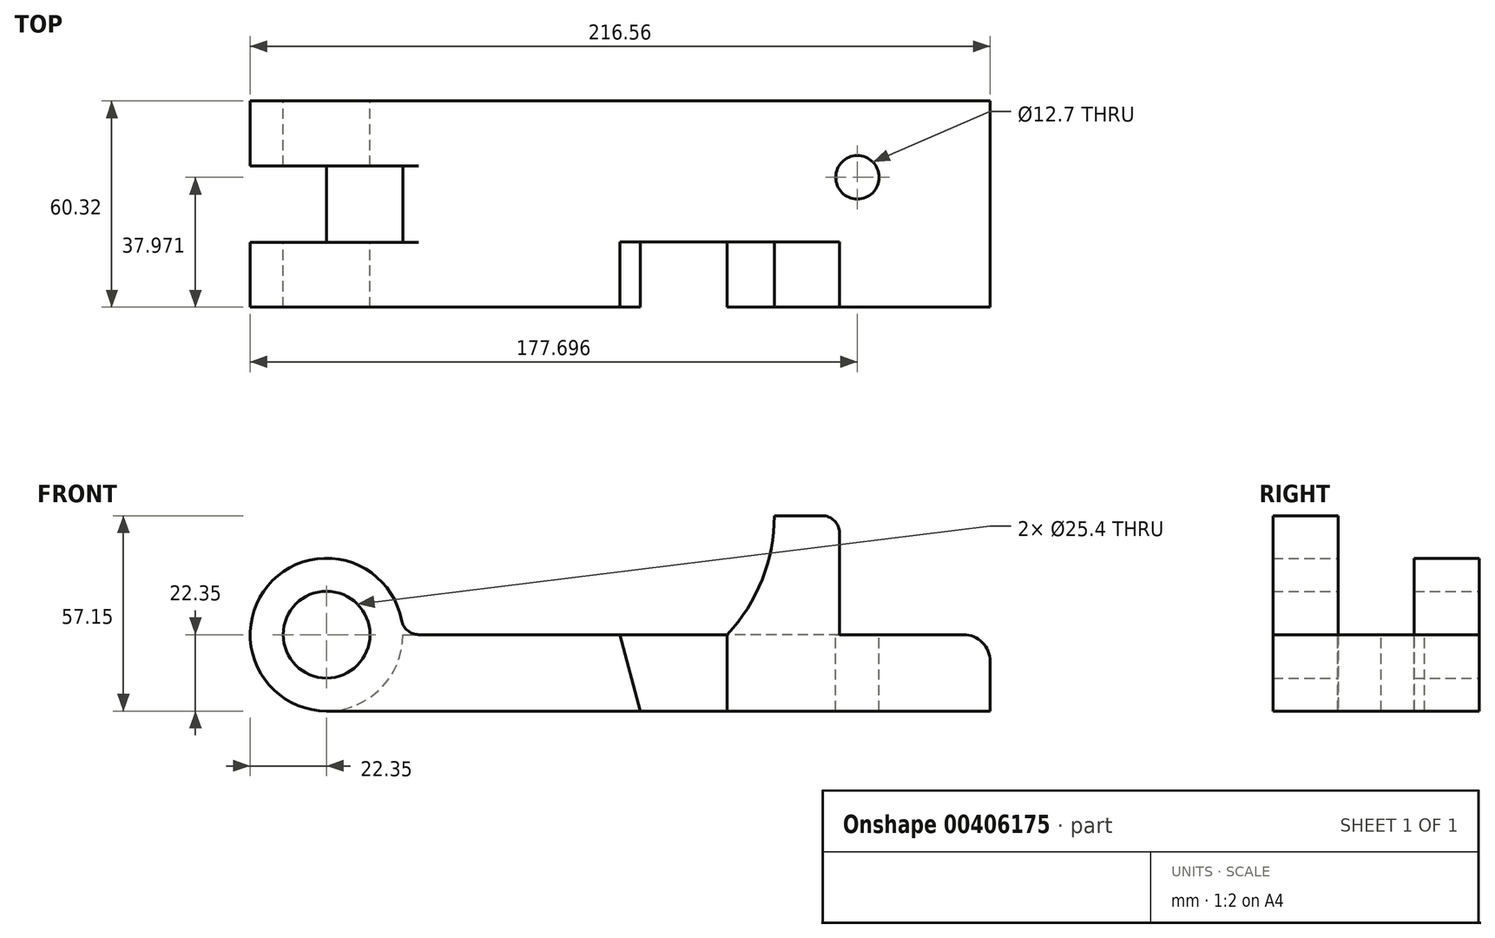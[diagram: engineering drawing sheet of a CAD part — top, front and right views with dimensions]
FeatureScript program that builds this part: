
annotation { "Feature Type Name" : "Feature", "Feature Type Description" : "" }
export const myFeature = defineFeature(function(context is Context, id is Id, definition is map)
    precondition{}
    {
        {
            var Q0;
            Q0=qCreatedBy(makeId("Front.planeOp"),FACE);
            var sketch = newSketch(context, id + "F0", { "sketchPlane" : qUnion([Q0])});
            skLineSegment(sketch, "E0.bottom", {"start": v(194.2, 0) * mm, "end": v(0, 0) * mm});
            skLineSegment(sketch, "E0.top", {"start": v(194.2, -22.35) * mm, "end": v(0, -22.35) * mm});
            skLineSegment(sketch, "E0.left", {"start": v(194.2, 0) * mm, "end": v(194.2, -22.35) * mm});
            skLineSegment(sketch, "E0.right", {"start": v(0, 0) * mm, "end": v(0, -22.35) * mm});
            skLineSegment(sketch, "E1.bottom", {"start": v(131.04, 0) * mm, "end": v(150.09, 0) * mm});
            skLineSegment(sketch, "E1.top", {"start": v(131.04, 34.8) * mm, "end": v(150.09, 34.8) * mm});
            skLineSegment(sketch, "E1.left", {"start": v(131.04, 0) * mm, "end": v(131.04, 34.8) * mm});
            skLineSegment(sketch, "E1.right", {"start": v(150.09, 0) * mm, "end": v(150.09, 34.8) * mm});
            skLineSegment(sketch, "E2", {"start": v(43.97, 0) * mm, "end": v(64.88, -22.35) * mm});
            skLineSegment(sketch, "E3", {"start": v(85.85, 0) * mm, "end": v(91.85, -22.35) * mm});
            skLineSegment(sketch, "E4", {"start": v(91.85, -22.35) * mm, "end": v(91.85, 0) * mm});
            skLineSegment(sketch, "E5", {"start": v(91.85, 0) * mm, "end": v(97.84, -22.35) * mm});
            skArc(sketch, "E6", {"start": v(117.25, 0) * mm, "mid": v(127.47, 16.08) * mm, "end": v(131.04, 34.8) * mm});
            skLineSegment(sketch, "E7", {"start": v(117.25, 0) * mm, "end": v(117.25, -22.35) * mm});
            skCircle(sketch, "E8", {"center": v(0, 0) * mm, "radius": 12.7 * mm});
            skCircle(sketch, "E9", {"center": v(0, 0) * mm, "radius": 22.35 * mm});
            skSolve(sketch);
        }
        {
            var Q0;
            {var subQ0=sQuery(id+"F0.wireOp",EDGE,"E5");Q0=makeQuery(id+"F0.imprint","IMPRINT",FACE,{"disambiguationData":[TD([[makeQuery(id+"F0.imprint","IMPRINT",EDGE,{"derivedFrom":subQ0}),1.0]])]});}
            var Q1;
            {var subQ0=sQuery(id+"F0.wireOp",EDGE,"E3");Q1=makeQuery(id+"F0.imprint","IMPRINT",FACE,{"disambiguationData":[TD([[makeQuery(id+"F0.imprint","IMPRINT",EDGE,{"derivedFrom":subQ0}),1.0]])]});}
            var Q2;
            {var subQ0=sQuery(id+"F0.wireOp",EDGE,"E2");Q2=makeQuery(id+"F0.imprint","IMPRINT",FACE,{"disambiguationData":[TD([[makeQuery(id+"F0.imprint","IMPRINT",EDGE,{"derivedFrom":subQ0}),1.0]])]});}
            var Q3;
            {var subQ0=sQuery(id+"F0.wireOp",EDGE,"E2");Q3=makeQuery(id+"F0.imprint","IMPRINT",FACE,{"disambiguationData":[TD([[makeQuery(id+"F0.imprint","IMPRINT",EDGE,{"derivedFrom":subQ0}),-1.0]])]});}
            var Q4;
            {var subQ0=sQuery(id+"F0.wireOp",EDGE,"E9");var subQ1=sQuery(id+"F0.wireOp",EDGE,"E0.bottom");var subQ2=makeQuery(id+"F0.imprint","INTERSECT",VERTEX,{"derivedFrom":[subQ1,subQ0]});Q4=makeQuery(id+"F0.imprint","IMPRINT",FACE,{"disambiguationData":[TD([[makeQuery(id+"F0.imprint","IMPRINT",EDGE,{"disambiguationData":[TD([[subQ2,-1.0]])],"derivedFrom":subQ1}),-1.0]])]});}
            var Q5;
            {var subQ0=sQuery(id+"F0.wireOp",EDGE,"E4");Q5=makeQuery(id+"F0.imprint","IMPRINT",FACE,{"disambiguationData":[TD([[makeQuery(id+"F0.imprint","IMPRINT",EDGE,{"derivedFrom":subQ0}),-1.0]])]});}
            var Q6;
            {var subQ0=sQuery(id+"F0.wireOp",EDGE,"E0.left");Q6=makeQuery(id+"F0.imprint","IMPRINT",FACE,{"disambiguationData":[TD([[makeQuery(id+"F0.imprint","IMPRINT",EDGE,{"derivedFrom":subQ0}),-1.0]])]});}
            var Q7;
            {var subQ0=sQuery(id+"F0.wireOp",EDGE,"E9");var subQ1=sQuery(id+"F0.wireOp",EDGE,"E0.bottom");var subQ2=makeQuery(id+"F0.imprint","INTERSECT",VERTEX,{"derivedFrom":[subQ1,subQ0]});Q7=makeQuery(id+"F0.imprint","IMPRINT",FACE,{"disambiguationData":[TD([[makeQuery(id+"F0.imprint","IMPRINT",EDGE,{"disambiguationData":[TD([[subQ2,-1.0]])],"derivedFrom":subQ1}),1.0]])]});}
            extrude(context, id + "F1", {"entities" : qUnion([Q0, Q1, Q2, Q3, Q4, Q5, Q6, Q7]), "endBound" : BoundingType.SYMMETRIC, "depth" : 60.32 * mm});
        }
        {
            var Q0;
            {var subQ0=sQuery(id+"F0.wireOp",EDGE,"E9");var subQ1=sQuery(id+"F0.wireOp",EDGE,"E0.bottom");var subQ2=makeQuery(id+"F0.imprint","INTERSECT",VERTEX,{"derivedFrom":[subQ1,subQ0]});Q0=makeQuery(id+"F0.imprint","IMPRINT",FACE,{"disambiguationData":[TD([[makeQuery(id+"F0.imprint","IMPRINT",EDGE,{"disambiguationData":[TD([[subQ2,-1.0]])],"derivedFrom":subQ1}),-1.0]])]});}
            var Q1;
            {var subQ0=sQuery(id+"F0.wireOp",EDGE,"E9");var subQ1=sQuery(id+"F0.wireOp",EDGE,"E0.bottom");var subQ2=makeQuery(id+"F0.imprint","INTERSECT",VERTEX,{"derivedFrom":[subQ1,subQ0]});Q1=makeQuery(id+"F0.imprint","IMPRINT",FACE,{"disambiguationData":[TD([[makeQuery(id+"F0.imprint","IMPRINT",EDGE,{"disambiguationData":[TD([[subQ2,-1.0]])],"derivedFrom":subQ1}),1.0]])]});}
            extrude(context, id + "F2", {"entities" : qUnion([Q0, Q1]), "operationType" : NewBodyOperationType.REMOVE, "endBound" : BoundingType.SYMMETRIC, "oppositeDirection" : true, "depth" : 22.33 * mm});
        }
        {
            var Q0;
            Q0=makeQuery(id+"F1.opExtrude","CAP_FACE",FACE,{"disambiguationData":[OSD([sQuery(id+"F0.wireOp",EDGE,"E0.bottom"),sQuery(id+"F0.wireOp",EDGE,"E0.top"),sQuery(id+"F0.wireOp",EDGE,"E0.left"),sQuery(id+"F0.wireOp",EDGE,"E1.top"),sQuery(id+"F0.wireOp",EDGE,"E1.right"),sQuery(id+"F0.wireOp",EDGE,"E6"),sQuery(id+"F0.wireOp",EDGE,"E8"),sQuery(id+"F0.wireOp",EDGE,"E9")])],"isStart":false});
            var sketch = newSketch(context, id + "F3", { "sketchPlane" : qUnion([Q0])});
            skLineSegment(sketch, "E10.0", {"start": v(117.25, 0) * mm, "end": v(117.25, -22.35) * mm});
            skLineSegment(sketch, "E11.0", {"start": v(85.85, 0) * mm, "end": v(91.85, -22.35) * mm});
            skLineSegment(sketch, "E12", {"start": v(85.85, 0) * mm, "end": v(117.25, 0) * mm});
            skLineSegment(sketch, "E13", {"start": v(91.85, -22.35) * mm, "end": v(117.25, -22.35) * mm});
            skLineSegment(sketch, "E14.0", {"start": v(150.09, 0) * mm, "end": v(150.09, 34.8) * mm});
            skPoint(sketch, "E15.0", {"position": v(140.56, 34.8) * mm});
            skLineSegment(sketch, "E16.0", {"start": v(131.04, 34.8) * mm, "end": v(150.09, 34.8) * mm});
            skArc(sketch, "E17.0", {"start": v(117.25, 0) * mm, "mid": v(127.47, 16.08) * mm, "end": v(131.04, 34.8) * mm});
            skLineSegment(sketch, "E18.0", {"start": v(194.2, 0) * mm, "end": v(0, 0) * mm});
            skSolve(sketch);
        }
        {
            var Q0;
            Q0=makeQuery(id+"F3.imprint","IMPRINT",FACE,{"disambiguationData":[TD([[makeQuery(id+"F3.imprint","IMPRINT",EDGE,{"derivedFrom":sQuery(id+"F3.wireOp",EDGE,"E10.0")}),-1.0]])]});
            extrude(context, id + "F4", {"entities" : qUnion([Q0]), "operationType" : NewBodyOperationType.REMOVE, "oppositeDirection" : true, "depth" : 19.05 * mm});
        }
        {
            var Q0;
            {var subQ0=sQuery(id+"F3.wireOp",EDGE,"E14.0");Q0=makeQuery(id+"F3.imprint","IMPRINT",FACE,{"disambiguationData":[TD([[makeQuery(id+"F3.imprint","IMPRINT",EDGE,{"derivedFrom":subQ0}),1.0]])]});}
            extrude(context, id + "F5", {"entities" : qUnion([Q0]), "operationType" : NewBodyOperationType.ADD, "oppositeDirection" : true, "depth" : 19.05 * mm});
        }
        {
            var Q0;
            Q0=makeQuery(id+"F1.opExtrude","SWEPT_EDGE",EDGE,{"disambiguationData":[OSD([sQuery(id+"F0.wireOp",EDGE,"E0.bottom"),sQuery(id+"F0.wireOp",EDGE,"E0.left")])]});
            fillet(context, id + "F6", {"entities" : qUnion([Q0]), "radius" : 7.87 * mm, "tangentPropagation" : true, "allowEdgeOverflow" : false});
        }
        {
            var Q0;
            Q0=makeQuery(id+"F5.opExtrude","SWEPT_EDGE",EDGE,{"disambiguationData":[OSD([sQuery(id+"F3.wireOp",EDGE,"E14.0"),sQuery(id+"F3.wireOp",EDGE,"E16.0")])]});
            var Q1;
            Q1=makeQuery(id+"F5.opExtrude","SWEPT_EDGE",EDGE,{"disambiguationData":[OSD([sQuery(id+"F3.wireOp",EDGE,"E14.0"),sQuery(id+"F3.wireOp",EDGE,"E18.0")])]});
            var Q2;
            {var subQ0=sQuery(id+"F0.wireOp",EDGE,"E9");var subQ1=sQuery(id+"F0.wireOp",EDGE,"E8");var subQ2=makeQuery(id+"F1.opExtrude","SWEPT_FACE",FACE,{"disambiguationData":[OSD([subQ0])]});var subQ3=sQuery(id+"F0.wireOp",EDGE,"E1.bottom");var subQ4=sQuery(id+"F0.wireOp",EDGE,"E0.bottom");var subQ5=makeQuery(id+"F1.opExtrude","SWEPT_FACE",FACE,{"disambiguationData":[OSD([subQ4,subQ3])]});Q2=makeQuery(id+"F2.boolean.opBoolean","SPLIT",EDGE,{"disambiguationData":[topologyDisambiguationEdgeConnected([subQ5,subQ2]),TD([makeQuery(id+"F2.opExtrude","CAP_FACE",FACE,{"disambiguationData":[OSD([subQ1,subQ0])],"isStart":false})])],"derivedFrom":makeQuery(id+"F1.opExtrude","SWEPT_EDGE",EDGE,{"disambiguationData":[OSD([subQ4,subQ0])]})});}
            var Q3;
            {var subQ0=sQuery(id+"F0.wireOp",EDGE,"E9");var subQ1=sQuery(id+"F0.wireOp",EDGE,"E8");var subQ2=sQuery(id+"F0.wireOp",EDGE,"E1.bottom");var subQ3=sQuery(id+"F0.wireOp",EDGE,"E0.bottom");var subQ4=makeQuery(id+"F1.opExtrude","SWEPT_FACE",FACE,{"disambiguationData":[OSD([subQ3,subQ2])]});var subQ5=makeQuery(id+"F1.opExtrude","SWEPT_FACE",FACE,{"disambiguationData":[OSD([subQ0])]});Q3=makeQuery(id+"F2.boolean.opBoolean","SPLIT",EDGE,{"disambiguationData":[topologyDisambiguationEdgeConnected([subQ4,subQ5]),TD([makeQuery(id+"F2.opExtrude","CAP_FACE",FACE,{"disambiguationData":[OSD([subQ1,subQ0])],"isStart":true})])],"derivedFrom":makeQuery(id+"F1.opExtrude","SWEPT_EDGE",EDGE,{"disambiguationData":[OSD([subQ3,subQ0])]})});}
            fillet(context, id + "F7", {"entities" : qUnion([Q0, Q1, Q2, Q3]), "radius" : 5.08 * mm, "tangentPropagation" : true, "allowEdgeOverflow" : false});
        }
        {
            var Q0;
            Q0=makeQuery(id+"F1.opExtrude","SWEPT_FACE",FACE,{"disambiguationData":[OSD([sQuery(id+"F0.wireOp",EDGE,"E0.bottom"),sQuery(id+"F0.wireOp",EDGE,"E1.bottom")])]});
            var sketch = newSketch(context, id + "F8", { "sketchPlane" : qUnion([Q0])});
            skCircle(sketch, "E19", {"center": v(155.35, 7.81) * mm, "radius": 6.35 * mm});
            skSolve(sketch);
        }
        {
            var Q0;
            Q0=makeQuery(id+"F8.imprint","IMPRINT",FACE,{"disambiguationData":[TD([[makeQuery(id+"F8.imprint","IMPRINT",EDGE,{"derivedFrom":sQuery(id+"F8.wireOp",EDGE,"E19")}),1.0]])]});
            extrude(context, id + "F9", {"entities" : qUnion([Q0]), "operationType" : NewBodyOperationType.REMOVE, "endBound" : BoundingType.THROUGH_ALL, "oppositeDirection" : true, "depth" : 25.4 * mm});
        }
    });
